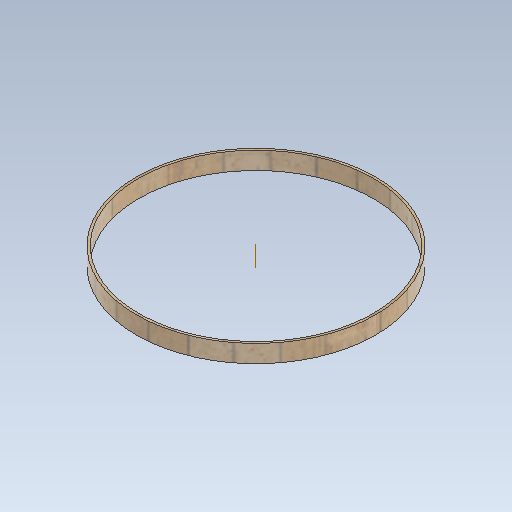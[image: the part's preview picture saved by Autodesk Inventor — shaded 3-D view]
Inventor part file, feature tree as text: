
AUTODESK INVENTOR PART (.ipt)
format: ipt  version: 2020 (Build 240168000, 168)  size: 136,704 bytes
history: native  units: mm
features: extrude x1, sketch x1
ambient origin geometry x8: Origin, YZ Plane, XZ Plane, XY Plane, X Axis, Y Axis, Z Axis, Center Point
bodies: Solid1 (feature_tree)
feature tree (2):
  extrude  "Extrusion1"  Depth=30.0mm TaperAngle=0.0deg
  sketch  "Sketch1"  dims[d0=400.0mm d1=30.0mm d2=0.0mm d20=408.0mm]
